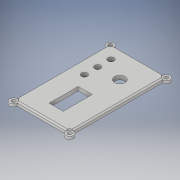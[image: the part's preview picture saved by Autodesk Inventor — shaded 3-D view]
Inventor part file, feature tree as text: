
AUTODESK INVENTOR PART (.ipt)
format: ipt  version: 2019 (Build 230136000, 136)  size: 220,160 bytes
history: native  units: mm
features: extrude x6, sketch x5, projected_geometry x3, chamfer x2
ambient origin geometry x8: Origin, YZ Plane, XZ Plane, XY Plane, X Axis, Y Axis, Z Axis, Center Point
bodies: Solid1 (feature_tree)
feature tree (16):
  extrude  "Extrusion1"  Depth=110.0mm
  extrude  "Extrusion2"  Depth=110.0mm
  extrude  "Extrusion3"  Depth=3.0mm
  extrude  "Extrusion4"  Depth=3.0mm TaperAngle=0.0deg
  sketch  "Sketch5"  dims[d24=16.0mm d25=33.0mm d26=24.0mm d27=24.0mm d28=16.5mm d29=3.0mm d30=0.0mm d31=6.8mm d32=6.8mm d33=6.8mm d34=15.125mm d35=15.125mm d36=15.125mm d37=15.125mm d38=6.0mm d39=0.0mm d40=20.0mm d42=110.0mm d43=20.0mm d45=64.0mm d48=1.5mm d49=0.0mm d50=1.5mm d51=2.0mm d52=45.0deg d53=16.0mm d54=55.0mm d55=12.0mm d56=23.0mm d58=1.5mm d59=0.0mm d60=1.5mm d61=2.0mm d62=45.0deg d64=30.0mm]
  extrude  "Extrusion6"  Depth=33.0mm
  chamfer  "Chamfer2"  Distance=24.0mm
  extrude  "Extrusion5"  Depth=24.0mm
  chamfer  "Chamfer1"  Distance=16.5mm
  sketch  "Sketch1"  dims[d0=64.0mm d1=110.0mm]
  sketch  "Sketch2"  dims[d2=8.485mm d3=20.0mm d5=110.0mm d6=20.0mm d8=64.0mm]
  projected_geometry  "Projected Loop1"
  sketch  "Sketch3"  dims[d11=3.0mm d12=0.0mm d13=4.3mm]
  sketch  "Sketch4"  dims[d14=20.0mm d16=110.0mm d17=20.0mm d19=64.0mm d22=3.0mm d23=0.0mm]
  projected_geometry  "Projected Loop2"
  projected_geometry  "Projected Loop3"
